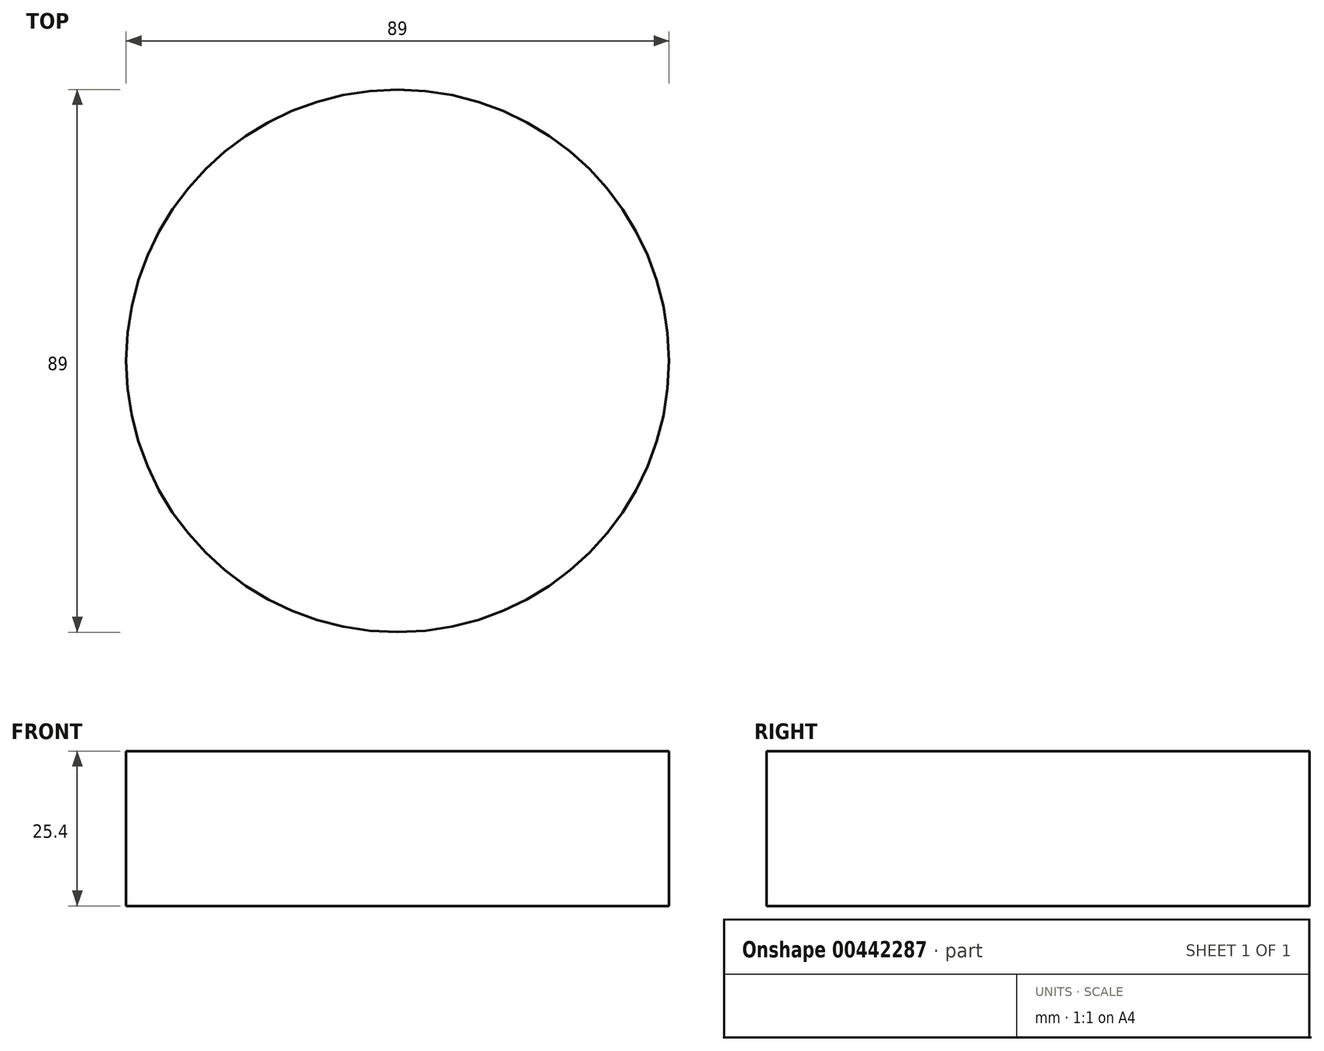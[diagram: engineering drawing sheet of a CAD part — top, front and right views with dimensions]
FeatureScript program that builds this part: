
annotation { "Feature Type Name" : "Feature", "Feature Type Description" : "" }
export const myFeature = defineFeature(function(context is Context, id is Id, definition is map)
    precondition{}
    {
        {
            var Q0;
            Q0=qCreatedBy(makeId("Top.planeOp"),FACE);
            var sketch = newSketch(context, id + "F0", { "sketchPlane" : qUnion([Q0])});
            skCircle(sketch, "E0", {"center": v(0, 0) * mm, "radius": 44.5 * mm});
            skSolve(sketch);
        }
        {
            var Q0;
            Q0=makeQuery(id+"F0.imprint","IMPRINT",FACE,{"disambiguationData":[TD([[makeQuery(id+"F0.imprint","IMPRINT",EDGE,{"derivedFrom":sQuery(id+"F0.wireOp",EDGE,"E0")}),1.0]])]});
            extrude(context, id + "F1", {"entities" : qUnion([Q0]), "depth" : 25.4 * mm});
        }
    });
